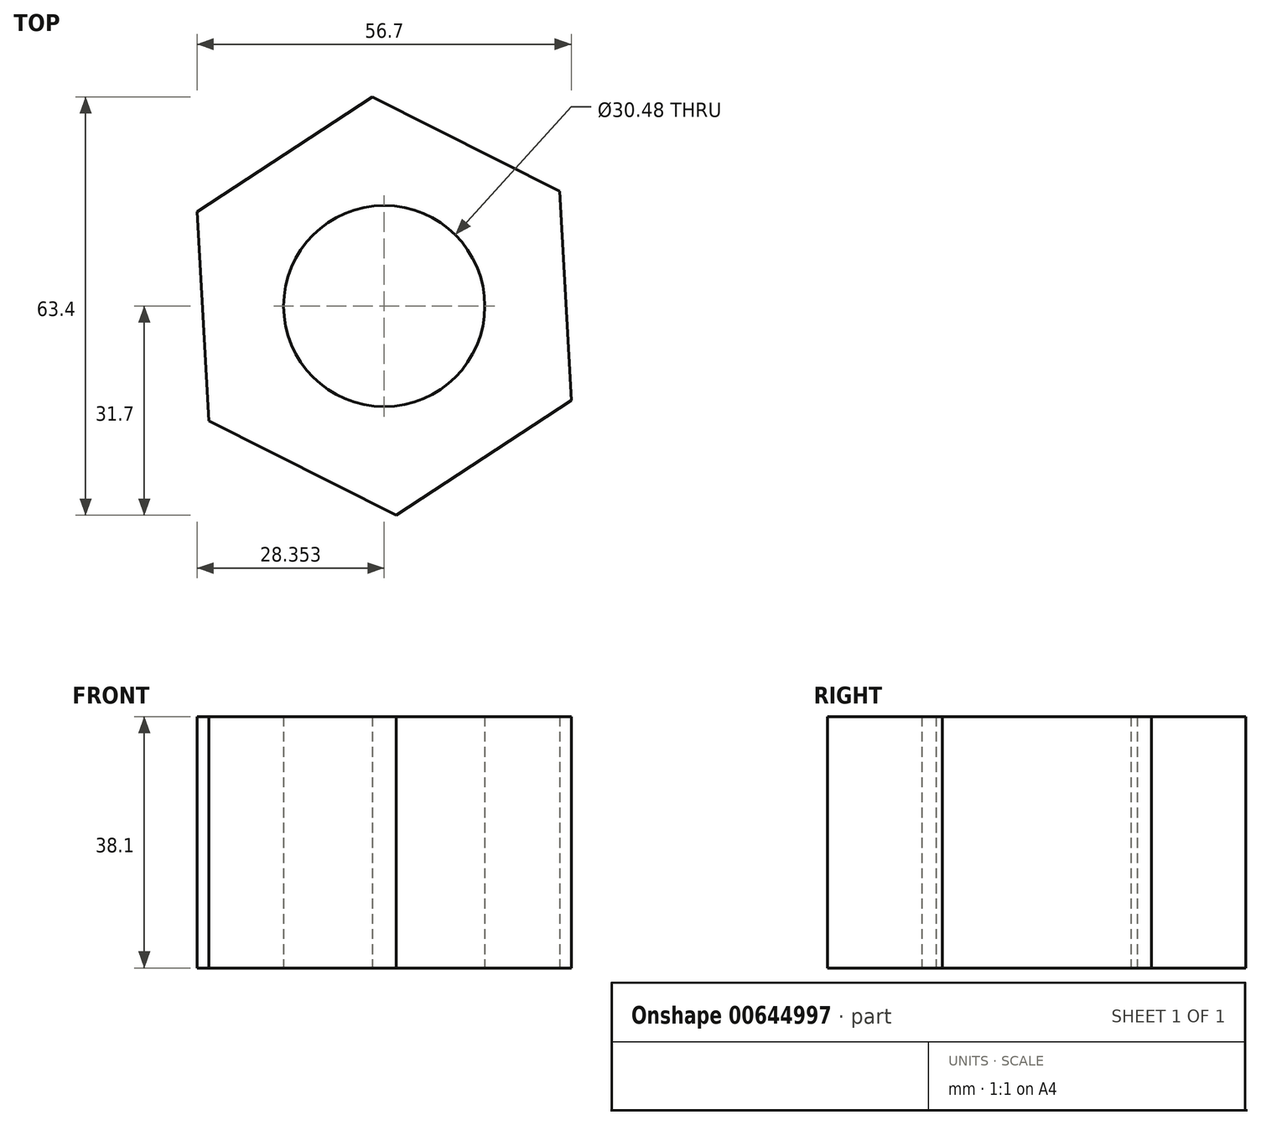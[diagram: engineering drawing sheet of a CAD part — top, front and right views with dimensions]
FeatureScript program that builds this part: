
annotation { "Feature Type Name" : "Feature", "Feature Type Description" : "" }
export const myFeature = defineFeature(function(context is Context, id is Id, definition is map)
    precondition{}
    {
        {
            var Q0;
            Q0=qCreatedBy(makeId("Top.planeOp"),FACE);
            var sketch = newSketch(context, id + "F0", { "sketchPlane" : qUnion([Q0])});
            skCircle(sketch, "E0.cCircle", {"center": v(23.7, 0) * mm, "radius": 31.75 * mm, "construction": true});
            skLineSegment(sketch, "E0.0", {"start": v(25.5, -31.7) * mm, "end": v(-2.85, -17.4) * mm});
            skLineSegment(sketch, "E0.1", {"start": v(-2.85, -17.4) * mm, "end": v(-4.65, 14.3) * mm});
            skLineSegment(sketch, "E0.2", {"start": v(-4.65, 14.3) * mm, "end": v(21.9, 31.7) * mm});
            skLineSegment(sketch, "E0.3", {"start": v(21.9, 31.7) * mm, "end": v(50.26, 17.4) * mm});
            skLineSegment(sketch, "E0.4", {"start": v(50.26, 17.4) * mm, "end": v(52.05, -14.3) * mm});
            skLineSegment(sketch, "E0.5", {"start": v(52.05, -14.3) * mm, "end": v(25.5, -31.7) * mm});
            skCircle(sketch, "E1", {"center": v(23.7, 0) * mm, "radius": 15.24 * mm});
            skSolve(sketch);
        }
        {
            var Q0;
            Q0 = qSketchRegion(id + "F0", true);
            extrude(context, id + "F1", {"entities" : qUnion([Q0]), "endBound" : BoundingType.SYMMETRIC, "depth" : 38.1 * mm, "offsetDistance" : 25.4 * mm});
        }
    });
